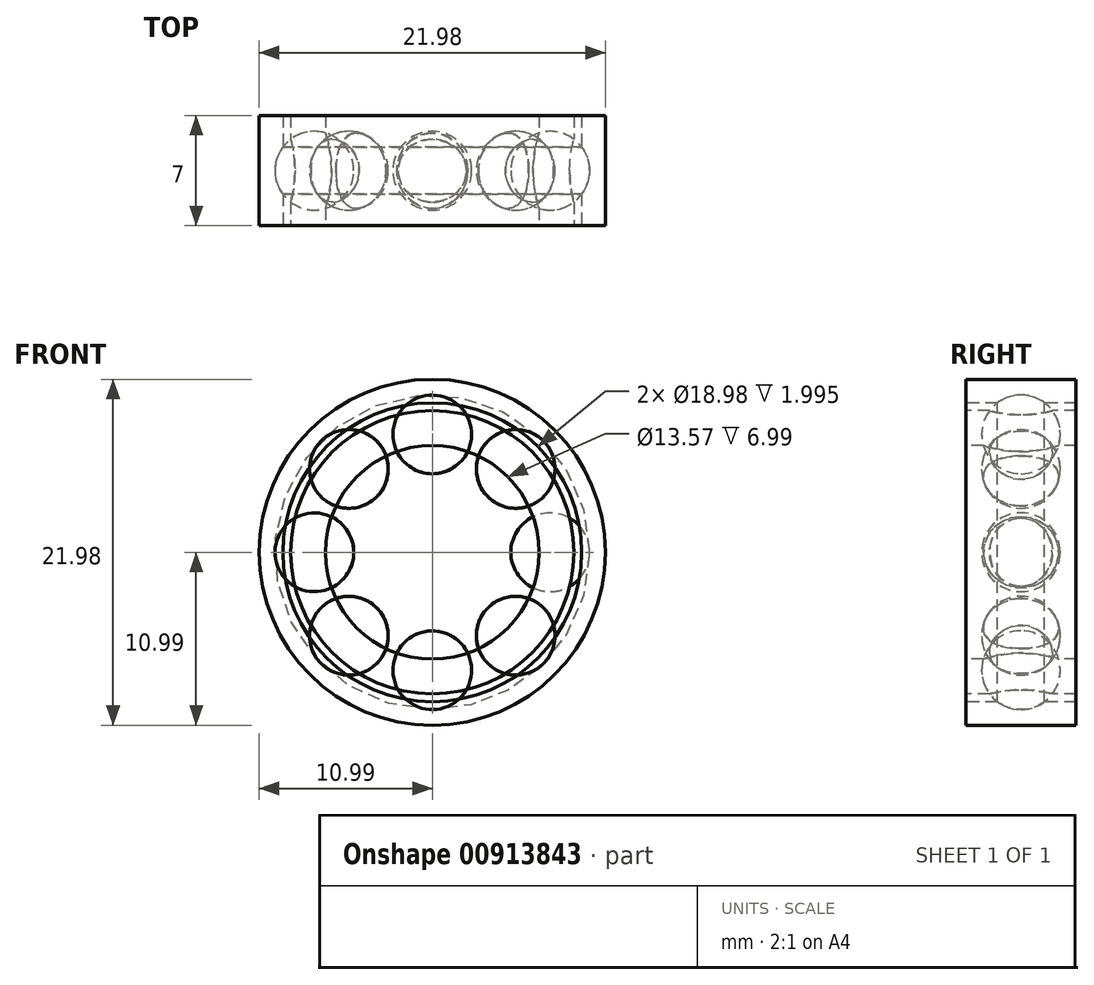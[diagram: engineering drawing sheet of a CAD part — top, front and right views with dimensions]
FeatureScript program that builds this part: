
annotation { "Feature Type Name" : "Feature", "Feature Type Description" : "" }
export const myFeature = defineFeature(function(context is Context, id is Id, definition is map)
    precondition{}
    {
        {
            assignVariable(context, id + "F0", {"variableType" : VariableType.NUMBER, "name" : "epaisseur", "numberValue" : 7});
        }
        {
            var Q0;
            Q0=qCreatedBy(makeId("Right.planeOp"),FACE);
            var sketch = newSketch(context, id + "F1", { "sketchPlane" : qUnion([Q0])});
            skLineSegment(sketch, "E0", {"start": v(-1.5, -9.5) * mm, "end": v(-3.5, -9.5) * mm});
            skLineSegment(sketch, "E1", {"start": v(-3.5, -9.5) * mm, "end": v(-3.5, -10.99) * mm});
            skLineSegment(sketch, "E2", {"start": v(-3.5, -10.99) * mm, "end": v(0, -10.99) * mm});
            skLineSegment(sketch, "E3", {"start": v(0, -10.99) * mm, "end": v(0, -9.99) * mm});
            skArc(sketch, "E4", {"start": v(-1.5, -9.49) * mm, "mid": v(-0.8, -9.86) * mm, "end": v(0, -9.99) * mm});
            skLineSegment(sketch, "E5.MirrorCS", {"start": v(3.5, -10.99) * mm, "end": v(0, -10.99) * mm});
            skArc(sketch, "E6.MirrorCS", {"start": v(1.5, -9.49) * mm, "mid": v(0.8, -9.86) * mm, "end": v(0, -9.99) * mm});
            skLineSegment(sketch, "E7.MirrorCS", {"start": v(1.5, -9.5) * mm, "end": v(3.5, -9.5) * mm});
            skLineSegment(sketch, "E8.MirrorCS", {"start": v(3.5, -9.5) * mm, "end": v(3.5, -10.99) * mm});
            skSolve(sketch);
        }
        {
            var Q0;
            Q0=qCreatedBy(makeId("Right.planeOp"),FACE);
            var sketch = newSketch(context, id + "F2", { "sketchPlane" : qUnion([Q0])});
            skArc(sketch, "E9", {"start": v(0, -4.99) * mm, "mid": v(-2.5, -7.49) * mm, "end": v(0, -9.99) * mm});
            skLineSegment(sketch, "E10", {"start": v(0, -9.99) * mm, "end": v(0, -4.99) * mm});
            skSolve(sketch);
        }
        {
            var Q0;
            Q0=qCreatedBy(makeId("Right.planeOp"),FACE);
            var sketch = newSketch(context, id + "F3", { "sketchPlane" : qUnion([Q0])});
            skArc(sketch, "E11", {"start": v(-1.5, -5.5) * mm, "mid": v(-0.8, -5.12) * mm, "end": v(0, -4.99) * mm});
            skLineSegment(sketch, "E12", {"start": v(-1.5, -5.5) * mm, "end": v(-3.5, -5.5) * mm});
            skLineSegment(sketch, "E13", {"start": v(-3.5, -5.5) * mm, "end": v(-3.5, -3.84) * mm});
            skLineSegment(sketch, "E14", {"start": v(-3.5, -3.84) * mm, "end": v(0, -3.84) * mm});
            skLineSegment(sketch, "E15", {"start": v(0, -3.84) * mm, "end": v(0, -4.99) * mm, "construction": true});
            skLineSegment(sketch, "E16.MirrorCS", {"start": v(1.5, -5.5) * mm, "end": v(3.5, -5.5) * mm});
            skArc(sketch, "E17.MirrorCS", {"start": v(1.5, -5.5) * mm, "mid": v(0.8, -5.12) * mm, "end": v(0, -4.99) * mm});
            skLineSegment(sketch, "E18.MirrorCS", {"start": v(3.5, -3.84) * mm, "end": v(0, -3.84) * mm});
            skLineSegment(sketch, "E19.MirrorCS", {"start": v(3.5, -5.5) * mm, "end": v(3.5, -3.84) * mm});
            skSolve(sketch);
        }
        {
            var Q0;
            Q0=makeQuery(id+"F2.imprint","IMPRINT",FACE,{"disambiguationData":[TD([[makeQuery(id+"F2.imprint","IMPRINT",EDGE,{"derivedFrom":sQuery(id+"F2.wireOp",EDGE,"E9")}),1.0]])]});
            var Q1;
            Q1=sQuery(id+"F2.wireOp",EDGE,"E10");
            revolve(context, id + "F4", {"surfaceOperationType" : NewSurfaceOperationType.NEW, "entities" : qUnion([Q0]), "axis" : qUnion([Q1]), "revolveType" : RevolveType.FULL});
        }
        {
            var Q0;
            Q0=qCreatedBy(makeId("Right.planeOp"),FACE);
            var sketch = newSketch(context, id + "F5", { "sketchPlane" : qUnion([Q0])});
            skLineSegment(sketch, "E20", {"start": v(-25.17, 0) * mm, "end": v(24.9, 0) * mm});
            skSolve(sketch);
        }
        {
            var Q0;
            Q0=makeQuery(id+"F1.imprint","IMPRINT",FACE,{"disambiguationData":[TD([[makeQuery(id+"F1.imprint","IMPRINT",EDGE,{"derivedFrom":sQuery(id+"F1.wireOp",EDGE,"E3")}),-1.0]])]});
            var Q1;
            Q1=makeQuery(id+"F3.imprint","IMPRINT",FACE,{"disambiguationData":[TD([[makeQuery(id+"F3.imprint","IMPRINT",EDGE,{"derivedFrom":sQuery(id+"F3.wireOp",EDGE,"E11")}),1.0]])]});
            var Q2;
            Q2=makeQuery(id+"F1.imprint","IMPRINT",FACE,{"disambiguationData":[TD([[makeQuery(id+"F1.imprint","IMPRINT",EDGE,{"derivedFrom":sQuery(id+"F1.wireOp",EDGE,"E0")}),1.0]])]});
            var Q3;
            Q3=sQuery(id+"F5.wireOp",EDGE,"E20");
            revolve(context, id + "F6", {"operationType" : NewBodyOperationType.ADD, "surfaceOperationType" : NewSurfaceOperationType.NEW, "entities" : qUnion([Q0, Q1, Q2]), "axis" : qUnion([Q3]), "revolveType" : RevolveType.FULL});
        }
        {
            var Q0;
            Q0=makeQuery(id+"F4.opRevolve","SWEPT_BODY",BODY,{"disambiguationData":[OSD([sQuery(id+"F2.wireOp",EDGE,"E9"),sQuery(id+"F2.wireOp",EDGE,"E10")])]});
            var Q1;
            Q1=sQuery(id+"F5.wireOp",EDGE,"E20");
            circularPattern(context, id + "F7", {"entities" : qUnion([Q0]), "axis" : qUnion([Q1]), "angle" : 360 * degree, "instanceCount" : 8, "equalSpace" : true});
        }
        {
            var Q0;
            Q0=makeQuery(id+"F6.opRevolve","SWEPT_FACE",FACE,{"disambiguationData":[OSD([sQuery(id+"F1.wireOp",EDGE,"E1")])]});
            var sketch = newSketch(context, id + "F8", { "sketchPlane" : qUnion([Q0])});
            skCircle(sketch, "E21", {"center": v(0, 0) * mm, "radius": 9 * mm});
            skCircle(sketch, "E22", {"center": v(0, 0) * mm, "radius": 6.78 * mm});
            skSolve(sketch);
        }
        {
            var Q0;
            Q0=makeQuery(id+"F8.imprint","IMPRINT",FACE,{"disambiguationData":[TD([[makeQuery(id+"F8.imprint","IMPRINT",EDGE,{"derivedFrom":sQuery(id+"F8.wireOp",EDGE,"E21")}),1.0]])]});
            extrude(context, id + "F9", {"entities" : qUnion([Q0]), "oppositeDirection" : true, "depth" : (getVariable(context, 'epaisseur')) * mm, "offsetDistance" : 25 * mm});
        }
        {
            var Q0;
            Q0=makeQuery(id+"F7.opPattern","COPY",BODY,{"derivedFrom":makeQuery(id+"F4.opRevolve","SWEPT_BODY",BODY,{"disambiguationData":[OSD([sQuery(id+"F2.wireOp",EDGE,"E9"),sQuery(id+"F2.wireOp",EDGE,"E10")])]}),"instanceName":"7"});
            var Q1;
            Q1=makeQuery(id+"F7.opPattern","COPY",BODY,{"derivedFrom":makeQuery(id+"F4.opRevolve","SWEPT_BODY",BODY,{"disambiguationData":[OSD([sQuery(id+"F2.wireOp",EDGE,"E9"),sQuery(id+"F2.wireOp",EDGE,"E10")])]}),"instanceName":"6"});
            var Q2;
            Q2=makeQuery(id+"F7.opPattern","COPY",BODY,{"derivedFrom":makeQuery(id+"F4.opRevolve","SWEPT_BODY",BODY,{"disambiguationData":[OSD([sQuery(id+"F2.wireOp",EDGE,"E9"),sQuery(id+"F2.wireOp",EDGE,"E10")])]}),"instanceName":"5"});
            var Q3;
            Q3=makeQuery(id+"F7.opPattern","COPY",BODY,{"derivedFrom":makeQuery(id+"F4.opRevolve","SWEPT_BODY",BODY,{"disambiguationData":[OSD([sQuery(id+"F2.wireOp",EDGE,"E9"),sQuery(id+"F2.wireOp",EDGE,"E10")])]}),"instanceName":"4"});
            var Q4;
            Q4=makeQuery(id+"F7.opPattern","COPY",BODY,{"derivedFrom":makeQuery(id+"F4.opRevolve","SWEPT_BODY",BODY,{"disambiguationData":[OSD([sQuery(id+"F2.wireOp",EDGE,"E9"),sQuery(id+"F2.wireOp",EDGE,"E10")])]}),"instanceName":"3"});
            var Q5;
            Q5=makeQuery(id+"F7.opPattern","COPY",BODY,{"derivedFrom":makeQuery(id+"F4.opRevolve","SWEPT_BODY",BODY,{"disambiguationData":[OSD([sQuery(id+"F2.wireOp",EDGE,"E9"),sQuery(id+"F2.wireOp",EDGE,"E10")])]}),"instanceName":"2"});
            var Q6;
            Q6=makeQuery(id+"F7.opPattern","COPY",BODY,{"derivedFrom":makeQuery(id+"F4.opRevolve","SWEPT_BODY",BODY,{"disambiguationData":[OSD([sQuery(id+"F2.wireOp",EDGE,"E9"),sQuery(id+"F2.wireOp",EDGE,"E10")])]}),"instanceName":"1"});
            var Q7;
            Q7=makeQuery(id+"F4.opRevolve","SWEPT_BODY",BODY,{"disambiguationData":[OSD([sQuery(id+"F2.wireOp",EDGE,"E9"),sQuery(id+"F2.wireOp",EDGE,"E10")])]});
            var Q8;
            Q8=makeQuery(id+"F9.opExtrude","SWEPT_BODY",BODY,{"disambiguationData":[OSD([sQuery(id+"F8.wireOp",EDGE,"E21"),sQuery(id+"F8.wireOp",EDGE,"E22")])]});
            booleanBodies(context, id + "F10", {"operationType" : BooleanOperationType.SUBTRACTION, "tools" : qUnion([Q0, Q1, Q2, Q3, Q4, Q5, Q6, Q7]), "targets" : qUnion([Q8]), "keepTools" : true});
        }
    });
